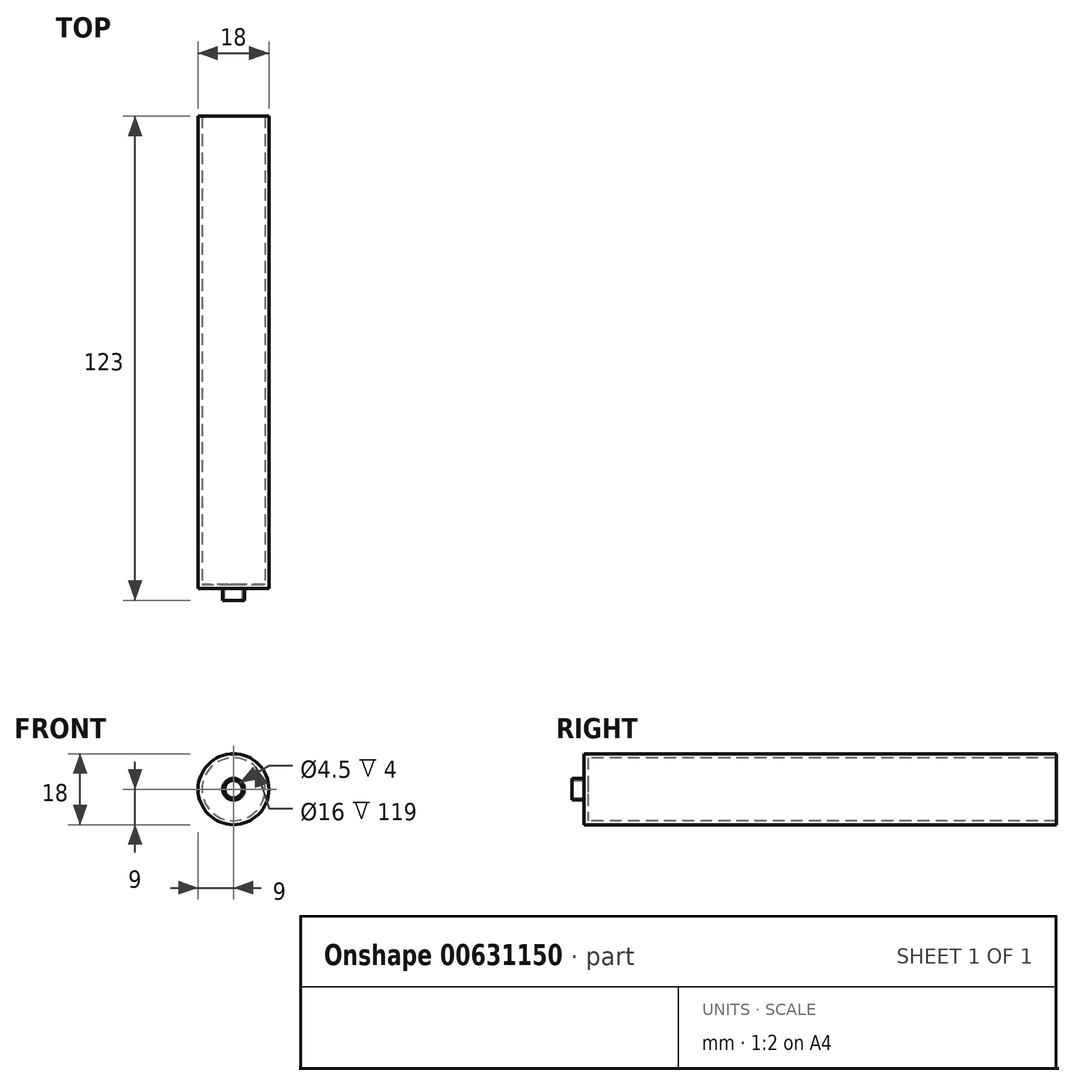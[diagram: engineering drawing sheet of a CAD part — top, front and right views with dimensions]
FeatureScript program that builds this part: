
annotation { "Feature Type Name" : "Feature", "Feature Type Description" : "" }
export const myFeature = defineFeature(function(context is Context, id is Id, definition is map)
    precondition{}
    {
        {
            var Q0;
            Q0=qCreatedBy(makeId("Front.planeOp"),FACE);
            var sketch = newSketch(context, id + "F0", { "sketchPlane" : qUnion([Q0])});
            skCircle(sketch, "E0", {"center": v(0, 0) * mm, "radius": 2.25 * mm});
            skCircle(sketch, "E1", {"center": v(0, 0) * mm, "radius": 2.75 * mm});
            skSolve(sketch);
        }
        {
            var Q0;
            Q0 = qSketchRegion(id + "F0", true);
            extrude(context, id + "F1", {"entities" : qUnion([Q0]), "depth" : 3 * mm, "offsetDistance" : 25 * mm});
        }
        {
            var Q0;
            Q0=makeQuery(id+"F1.opExtrude","CAP_FACE",FACE,{"disambiguationData":[OSD([sQuery(id+"F0.wireOp",EDGE,"E0"),sQuery(id+"F0.wireOp",EDGE,"E1")])],"isStart":true});
            var sketch = newSketch(context, id + "F2", { "sketchPlane" : qUnion([Q0])});
            skCircle(sketch, "E2", {"center": v(0, 0) * mm, "radius": 9 * mm});
            skSolve(sketch);
        }
        {
            var Q0;
            Q0 = qSketchRegion(id + "F2", true);
            extrude(context, id + "F3", {"entities" : qUnion([Q0]), "operationType" : NewBodyOperationType.ADD, "depth" : 120 * mm, "offsetDistance" : 25 * mm});
        }
        {
            var Q0;
            Q0=makeQuery(id+"F3.opExtrude","CAP_FACE",FACE,{"disambiguationData":[OSD([sQuery(id+"F2.wireOp",EDGE,"E2")])],"isStart":false});
            shell(context, id + "F4", {"entities" : qUnion([Q0]), "thickness" : 1 * mm});
        }
        {
            var Q0;
            Q0=makeQuery(id+"F0.imprint","IMPRINT",FACE,{"disambiguationData":[TD([[makeQuery(id+"F0.imprint","IMPRINT",EDGE,{"derivedFrom":sQuery(id+"F0.wireOp",EDGE,"E0")}),1.0]])]});
            extrude(context, id + "F5", {"entities" : qUnion([Q0]), "operationType" : NewBodyOperationType.REMOVE, "oppositeDirection" : true, "depth" : 25 * mm, "offsetDistance" : 25 * mm});
        }
    });
